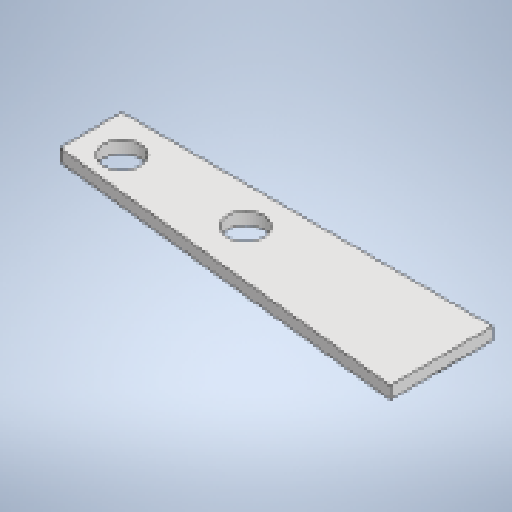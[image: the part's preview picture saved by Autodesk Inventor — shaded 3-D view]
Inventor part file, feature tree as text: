
AUTODESK INVENTOR PART (.ipt)
format: ipt  version: 2025.1 (Build 291241020, 241B)  size: 228,352 bytes
history: native  units: mm
features: other x4, sketch x3, sheet_metal_op x1, extrude x1, projected_geometry x1
ambient origin geometry x8: Origin, YZ Plane, XZ Plane, XY Plane, X Axis, Y Axis, Z Axis, Center Point
bodies: Solid1 (feature_tree)
feature tree (10):
  sheet_metal_op  "Face1"
  sketch  "Sketch6"  dims[d43=10.0mm d44=60.0mm d45=6.0mm d46=6.0mm d47=6.0mm d48=20.0mm d49=0.0mm d50=0.0mm d51=1.094509mm]
  other  "Mark1"
  other  "A-Side Definition"
  extrude  "Extrusion1"  Depth=200.0mm
  sketch  "Sketch1"  dims[d2=2.0mm d6=200.0mm]
  other  "Plate1"
  sketch  "Sketch2"  dims[d9=20.0mm]
  projected_geometry  "Projected Loop3"
  other  "Definition1"
